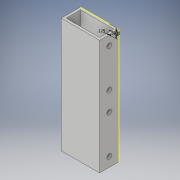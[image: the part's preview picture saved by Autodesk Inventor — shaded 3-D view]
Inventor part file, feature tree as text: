
AUTODESK INVENTOR PART (.ipt)
format: ipt  version: 2017 (Build 210142000, 142)  size: 129,536 bytes
history: native  units: in
note: dims shown in document units (in); Inventor stores cm internally (conversion verified against a paired STEP export)
features: sketch x3, extrude x1, hole x1
ambient origin geometry x8: Origin, YZ Plane, XZ Plane, XY Plane, X Axis, Y Axis, Z Axis, Center Point
bodies: Solid1 (feature_tree)
feature tree (5):
  extrude  "Extrusion1"  Depth=1.0in
  hole  "Hole2"  [1 undecoded]
  sketch  "Sketch3"  dims[d4=0.125in d5=0.125in d6=6.0in d7=0.0in d8=0.25in d9=0.5in d10=0.25in d11=0.5in d19=0.25in d20=0.75in d21=0.375in d22=0.25in d23=0.5635in d24=1.0in d25=0.8108in d27=0.5in d28=0.5in d30=0.125in]
  sketch  "Sketch1"  dims[d0=2.0in d1=1.0in]
  sketch  "Sketch2"  dims[d2=1.75in d3=0.75in]
note: 1 required parameter value undecoded (feature->parameter linkage not recoverable at this tier; creation-order binding heuristic only, values carry confidence <= 0.55)
